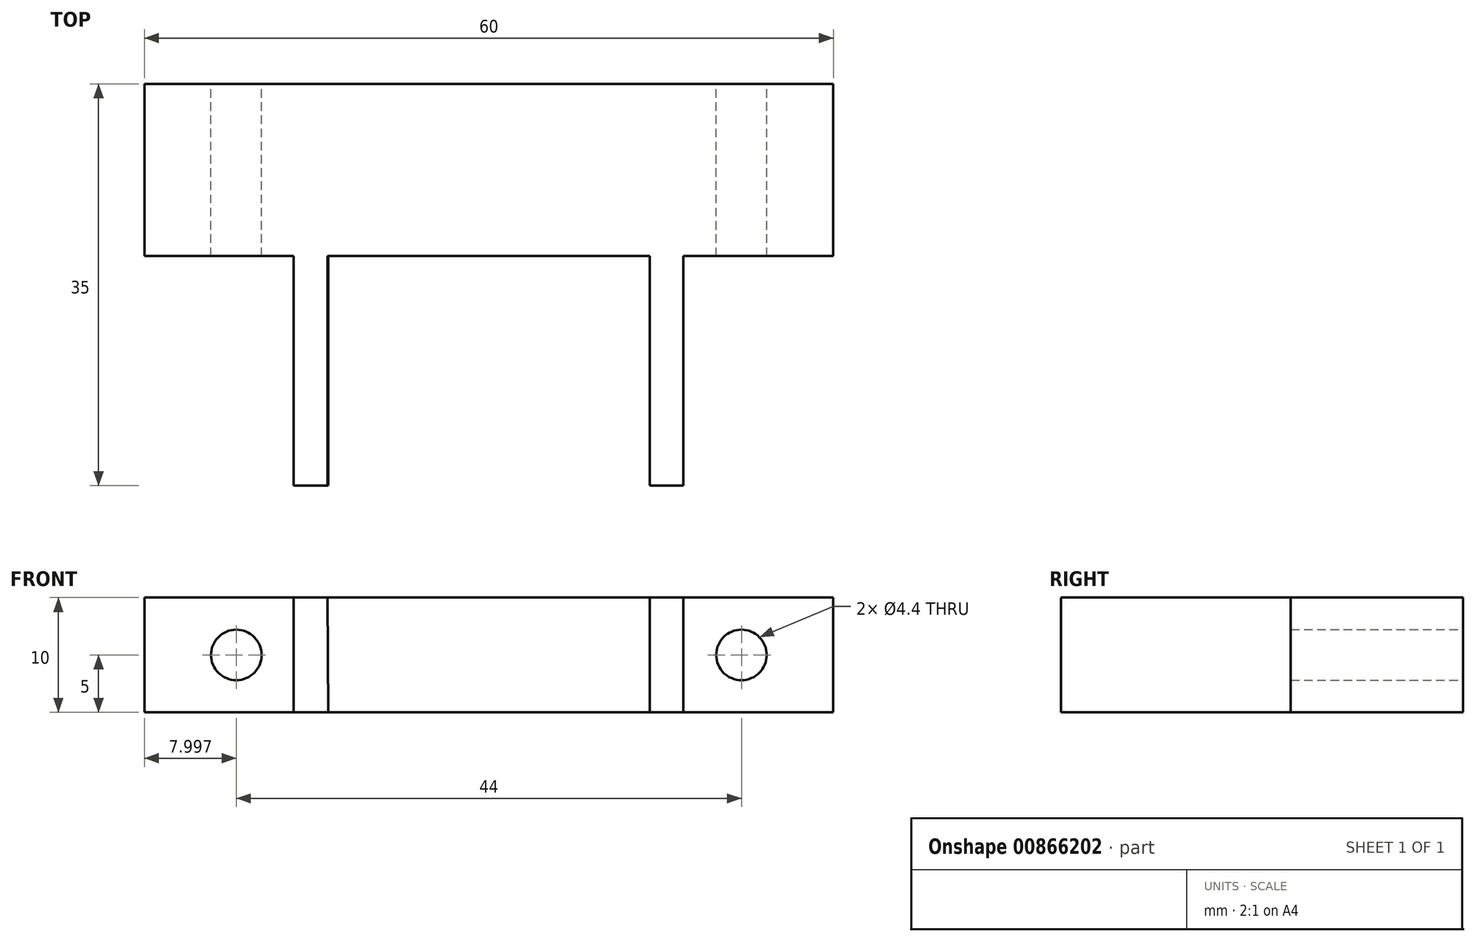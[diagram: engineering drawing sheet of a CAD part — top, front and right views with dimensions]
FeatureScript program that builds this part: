
annotation { "Feature Type Name" : "Feature", "Feature Type Description" : "" }
export const myFeature = defineFeature(function(context is Context, id is Id, definition is map)
    precondition{}
    {
        {
            var Q0;
            Q0=qCreatedBy(makeId("Front.planeOp"),FACE);
            var sketch = newSketch(context, id + "F0", { "sketchPlane" : qUnion([Q0])});
            skLineSegment(sketch, "E0.bottom", {"start": v(-61.43, 10) * mm, "end": v(-1.43, 10) * mm});
            skLineSegment(sketch, "E0.top", {"start": v(-61.43, 0) * mm, "end": v(-45.43, 0) * mm});
            skLineSegment(sketch, "E0.left", {"start": v(-61.43, 10) * mm, "end": v(-61.43, 0) * mm});
            skLineSegment(sketch, "E0.right", {"start": v(-1.43, 10) * mm, "end": v(-1.43, 0) * mm});
            skLineSegment(sketch, "E1", {"start": v(-45.43, 10) * mm, "end": v(-45.43, 0) * mm});
            skLineSegment(sketch, "E2", {"start": v(-17.43, 0) * mm, "end": v(-17.43, 10) * mm});
            skLineSegment(sketch, "E3.trimOffspring", {"start": v(-17.43, 0) * mm, "end": v(-1.43, 0) * mm});
            skLineSegment(sketch, "E4", {"start": v(-45.43, 0) * mm, "end": v(-17.43, 0) * mm});
            skLineSegment(sketch, "E5", {"start": v(-48.43, 10) * mm, "end": v(-48.43, 0) * mm});
            skLineSegment(sketch, "E6", {"start": v(-14.43, 10) * mm, "end": v(-14.43, 0) * mm});
            skCircle(sketch, "E7", {"center": v(-53.43, 5) * mm, "radius": 2.2 * mm});
            skPoint(sketch, "E7.centerSnap0", {"position": v(-53.43, 0) * mm});
            skPoint(sketch, "E7.centerSnap1", {"position": v(-61.43, 5) * mm});
            skCircle(sketch, "E8", {"center": v(-9.43, 5) * mm, "radius": 2.2 * mm});
            skPoint(sketch, "E8.centerSnap0", {"position": v(-1.43, 5) * mm});
            skPoint(sketch, "E8.centerSnap1", {"position": v(-9.43, 0) * mm});
            skSolve(sketch);
        }
        {
            var Q0;
            Q0 = qSketchRegion(id + "F0", true);
            extrude(context, id + "F1", {"entities" : qUnion([Q0]), "depth" : 15 * mm, "offsetDistance" : 25 * mm});
        }
        {
            var Q0;
            Q0=makeQuery(id+"F1.opExtrude","CAP_FACE",FACE,{"disambiguationData":[OSD([sQuery(id+"F0.wireOp",EDGE,"E0.bottom"),sQuery(id+"F0.wireOp",EDGE,"E0.top"),sQuery(id+"F0.wireOp",EDGE,"E0.left"),sQuery(id+"F0.wireOp",EDGE,"E0.right"),sQuery(id+"F0.wireOp",EDGE,"E3.trimOffspring"),sQuery(id+"F0.wireOp",EDGE,"E4"),sQuery(id+"F0.wireOp",EDGE,"E7"),sQuery(id+"F0.wireOp",EDGE,"E8")])],"isStart":false});
            var sketch = newSketch(context, id + "F2", { "sketchPlane" : qUnion([Q0])});
            skLineSegment(sketch, "E9.0", {"start": v(-48.45, 10) * mm, "end": v(-14.49, 10) * mm});
            skLineSegment(sketch, "E10.0", {"start": v(-45.43, 0) * mm, "end": v(-17.43, 0) * mm});
            skLineSegment(sketch, "E11.0", {"start": v(-61.43, 0) * mm, "end": v(-45.43, 0) * mm});
            skLineSegment(sketch, "E12.0", {"start": v(-17.43, 0) * mm, "end": v(-1.43, 0) * mm});
            skLineSegment(sketch, "E13", {"start": v(-45.5, 10) * mm, "end": v(-45.43, 0) * mm});
            skLineSegment(sketch, "E14", {"start": v(-17.43, 0) * mm, "end": v(-17.43, 10) * mm});
            skLineSegment(sketch, "E15", {"start": v(-17.43, 10) * mm, "end": v(-14.49, 10) * mm});
            skLineSegment(sketch, "E16", {"start": v(-14.49, 10) * mm, "end": v(-14.49, 0) * mm});
            skLineSegment(sketch, "E17", {"start": v(-14.49, 0) * mm, "end": v(-17.43, 0) * mm});
            skLineSegment(sketch, "E18", {"start": v(-45.5, 10) * mm, "end": v(-48.45, 10) * mm});
            skLineSegment(sketch, "E19", {"start": v(-48.45, 10) * mm, "end": v(-48.45, 0) * mm});
            skLineSegment(sketch, "E20", {"start": v(-48.45, 0) * mm, "end": v(-45.43, 0) * mm});
            skPoint(sketch, "E21.orphan", {"position": v(-61.43, 10) * mm});
            skPoint(sketch, "E22.orphan", {"position": v(-1.43, 10) * mm});
            skSolve(sketch);
        }
        {
            var Q0;
            Q0=makeQuery(id+"F2.imprint","IMPRINT",FACE,{"disambiguationData":[TD([[makeQuery(id+"F2.imprint","IMPRINT",EDGE,{"derivedFrom":sQuery(id+"F2.wireOp",EDGE,"E13")}),-1.0]])]});
            var Q1;
            Q1=makeQuery(id+"F2.imprint","IMPRINT",FACE,{"disambiguationData":[TD([[makeQuery(id+"F2.imprint","IMPRINT",EDGE,{"derivedFrom":sQuery(id+"F2.wireOp",EDGE,"E14")}),-1.0]])]});
            extrude(context, id + "F3", {"entities" : qUnion([Q0, Q1]), "operationType" : NewBodyOperationType.ADD, "depth" : 20 * mm, "offsetDistance" : 25 * mm});
        }
    });
